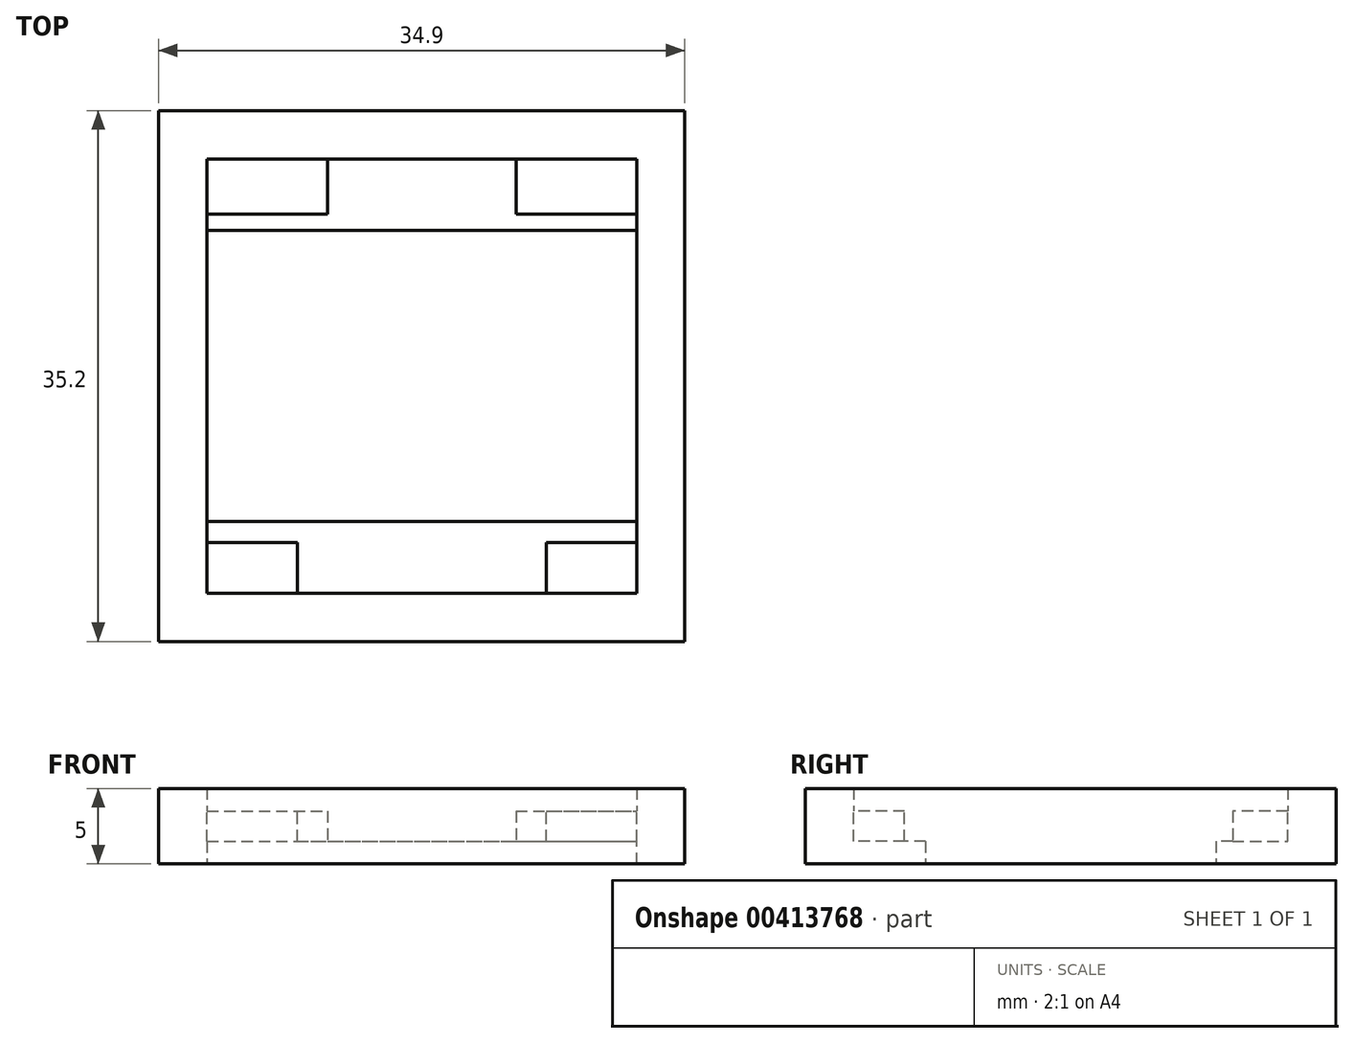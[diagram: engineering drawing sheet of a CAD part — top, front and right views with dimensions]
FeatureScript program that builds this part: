
annotation { "Feature Type Name" : "Feature", "Feature Type Description" : "" }
export const myFeature = defineFeature(function(context is Context, id is Id, definition is map)
    precondition{}
    {
        {
            var Q0;
            Q0=qCreatedBy(makeId("Top.planeOp"),FACE);
            var sketch = newSketch(context, id + "F0", { "sketchPlane" : qUnion([Q0])});
            skLineSegment(sketch, "E0.bottom", {"start": v(-14.25, 14.4) * mm, "end": v(14.25, 14.4) * mm});
            skLineSegment(sketch, "E0.top", {"start": v(-14.25, -14.4) * mm, "end": v(14.25, -14.4) * mm});
            skLineSegment(sketch, "E0.left", {"start": v(-14.25, 14.4) * mm, "end": v(-14.25, -14.4) * mm});
            skLineSegment(sketch, "E0.right", {"start": v(14.25, 14.4) * mm, "end": v(14.25, -14.4) * mm});
            skPoint(sketch, "E0.middle", {"position": v(0, 0) * mm});
            skLineSegment(sketch, "E1.0", {"start": v(17.45, 17.6) * mm, "end": v(17.45, -17.6) * mm});
            skLineSegment(sketch, "E1.1", {"start": v(-17.45, 17.6) * mm, "end": v(17.45, 17.6) * mm});
            skLineSegment(sketch, "E1.2", {"start": v(-17.45, 17.6) * mm, "end": v(-17.45, -17.6) * mm});
            skLineSegment(sketch, "E1.3", {"start": v(-17.45, -17.6) * mm, "end": v(17.45, -17.6) * mm});
            skCircle(sketch, "E2", {"center": v(11.65, -12.4) * mm, "radius": 1.75 * mm, "construction": true});
            skCircle(sketch, "E3", {"center": v(11.65, 11.4) * mm, "radius": 1.75 * mm, "construction": true});
            skCircle(sketch, "E4", {"center": v(-11.65, 11.4) * mm, "radius": 1.75 * mm, "construction": true});
            skCircle(sketch, "E5", {"center": v(-11.65, -12.4) * mm, "radius": 1.75 * mm, "construction": true});
            skLineSegment(sketch, "E6.bottom", {"start": v(-14.25, 9.65) * mm, "end": v(14.25, 9.65) * mm});
            skLineSegment(sketch, "E6.top", {"start": v(-14.25, -9.63) * mm, "end": v(14.25, -9.63) * mm});
            skLineSegment(sketch, "E6.left", {"start": v(-14.25, 9.65) * mm, "end": v(-14.25, -9.63) * mm});
            skLineSegment(sketch, "E6.right", {"start": v(14.25, 9.65) * mm, "end": v(14.25, -9.63) * mm});
            skSolve(sketch);
        }
        {
            var Q0;
            {var subQ4=sQuery(id+"F0.wireOp",EDGE,"E0.bottom");Q0=makeQuery(id+"F0.imprint","IMPRINT",FACE,{"disambiguationData":[TD([[makeQuery(id+"F0.imprint","IMPRINT",EDGE,{"derivedFrom":subQ4}),1.0]])]});}
            extrude(context, id + "F1", {"entities" : qUnion([Q0]), "depth" : 5 * mm, "offsetDistance" : 25 * mm});
        }
        {
            var Q0;
            Q0=qCreatedBy(makeId("Top.planeOp"),FACE);
            var sketch = newSketch(context, id + "F2", { "sketchPlane" : qUnion([Q0])});
            skLineSegment(sketch, "E7.bottom", {"start": v(-14.25, 14.4) * mm, "end": v(14.25, 14.4) * mm});
            skLineSegment(sketch, "E7.top", {"start": v(-14.25, -14.4) * mm, "end": v(14.25, -14.4) * mm});
            skLineSegment(sketch, "E7.left", {"start": v(-14.25, 14.4) * mm, "end": v(-14.25, -14.4) * mm});
            skLineSegment(sketch, "E7.right", {"start": v(14.25, 14.4) * mm, "end": v(14.25, -14.4) * mm});
            skPoint(sketch, "E7.middle", {"position": v(0, 0) * mm});
            skCircle(sketch, "E8", {"center": v(12.25, -12.4) * mm, "radius": 1.75 * mm, "construction": true});
            skCircle(sketch, "E9", {"center": v(11.05, 11.4) * mm, "radius": 1.75 * mm, "construction": true});
            skCircle(sketch, "E10", {"center": v(-12.25, 11.4) * mm, "radius": 1.75 * mm, "construction": true});
            skCircle(sketch, "E11", {"center": v(-11.05, -12.4) * mm, "radius": 1.75 * mm, "construction": true});
            skLineSegment(sketch, "E12.bottom", {"start": v(-14.25, 9.65) * mm, "end": v(14.25, 9.65) * mm});
            skLineSegment(sketch, "E12.top", {"start": v(-14.25, -9.63) * mm, "end": v(14.25, -9.63) * mm});
            skLineSegment(sketch, "E12.left", {"start": v(-14.25, 9.65) * mm, "end": v(-14.25, -9.63) * mm});
            skLineSegment(sketch, "E12.right", {"start": v(14.25, 9.65) * mm, "end": v(14.25, -9.63) * mm});
            skSolve(sketch);
        }
        {
            var Q0;
            {var subQ0=sQuery(id+"F2.wireOp",EDGE,"E7.bottom");Q0=makeQuery(id+"F2.imprint","IMPRINT",FACE,{"disambiguationData":[TD([[makeQuery(id+"F2.imprint","IMPRINT",EDGE,{"derivedFrom":subQ0}),-1.0]])]});}
            var Q1;
            {var subQ0=sQuery(id+"F2.wireOp",EDGE,"E7.top");Q1=makeQuery(id+"F2.imprint","IMPRINT",FACE,{"disambiguationData":[TD([[makeQuery(id+"F2.imprint","IMPRINT",EDGE,{"derivedFrom":subQ0}),1.0]])]});}
            extrude(context, id + "F3", {"entities" : qUnion([Q0, Q1]), "operationType" : NewBodyOperationType.ADD, "depth" : 3.5 * mm, "offsetDistance" : 25 * mm});
        }
        {
            var Q0;
            Q0=qCreatedBy(makeId("Top.planeOp"),FACE);
            cPlane(context, id + "F4", {"entities" : qUnion([Q0]), "cplaneType" : CPlaneType.OFFSET, "offset" : 3.5 * mm, "width" : 150 * mm, "height" : 150 * mm});
        }
        {
            var Q0;
            Q0=qCreatedBy(id+"F4.planeOp",FACE);
            var sketch = newSketch(context, id + "F5", { "sketchPlane" : qUnion([Q0])});
            skLineSegment(sketch, "E13", {"start": v(-6.25, 27.74) * mm, "end": v(-6.25, -4.9) * mm, "construction": true});
            skLineSegment(sketch, "E14", {"start": v(6.25, 21.83) * mm, "end": v(6.25, 6.4) * mm, "construction": true});
            skLineSegment(sketch, "E15", {"start": v(-8.25, -5.52) * mm, "end": v(-8.25, -18.12) * mm, "construction": true});
            skLineSegment(sketch, "E16", {"start": v(8.25, -5.91) * mm, "end": v(8.25, -17.84) * mm, "construction": true});
            skLineSegment(sketch, "E17.bottom", {"start": v(-6.25, 9.65) * mm, "end": v(6.25, 9.65) * mm});
            skLineSegment(sketch, "E17.top", {"start": v(-6.25, 14.4) * mm, "end": v(6.25, 14.4) * mm});
            skLineSegment(sketch, "E17.left", {"start": v(-6.25, 9.65) * mm, "end": v(-6.25, 14.4) * mm});
            skLineSegment(sketch, "E17.right", {"start": v(6.25, 9.65) * mm, "end": v(6.25, 14.4) * mm});
            skLineSegment(sketch, "E18.bottom", {"start": v(-8.25, -9.63) * mm, "end": v(8.25, -9.63) * mm});
            skLineSegment(sketch, "E18.top", {"start": v(-8.25, -14.4) * mm, "end": v(8.25, -14.4) * mm});
            skLineSegment(sketch, "E18.left", {"start": v(-8.25, -9.63) * mm, "end": v(-8.25, -14.4) * mm});
            skLineSegment(sketch, "E18.right", {"start": v(8.25, -9.63) * mm, "end": v(8.25, -14.4) * mm});
            skSolve(sketch);
        }
        {
            var Q0;
            Q0=qSketchRegion(id+"F5",true);
            extrude(context, id + "F6", {"entities" : qUnion([Q0]), "operationType" : NewBodyOperationType.REMOVE, "oppositeDirection" : true, "depth" : 2 * mm, "offsetDistance" : 25 * mm});
        }
        {
            var Q0;
            Q0=qCreatedBy(id+"F4.planeOp",FACE);
            var sketch = newSketch(context, id + "F7", { "sketchPlane" : qUnion([Q0])});
            skLineSegment(sketch, "E19.bottom", {"start": v(-14.25, 10.74) * mm, "end": v(14.25, 10.74) * mm});
            skLineSegment(sketch, "E19.top", {"start": v(-14.25, 9.54) * mm, "end": v(14.25, 9.54) * mm});
            skLineSegment(sketch, "E19.left", {"start": v(-14.25, 10.74) * mm, "end": v(-14.25, 9.54) * mm});
            skLineSegment(sketch, "E19.right", {"start": v(14.25, 10.74) * mm, "end": v(14.25, 9.54) * mm});
            skLineSegment(sketch, "E20.bottom", {"start": v(-14.25, -9.63) * mm, "end": v(14.25, -9.63) * mm});
            skLineSegment(sketch, "E20.top", {"start": v(-14.25, -11.03) * mm, "end": v(14.25, -11.03) * mm});
            skLineSegment(sketch, "E20.left", {"start": v(-14.25, -9.63) * mm, "end": v(-14.25, -11.03) * mm});
            skLineSegment(sketch, "E20.right", {"start": v(14.25, -9.63) * mm, "end": v(14.25, -11.03) * mm});
            skSolve(sketch);
        }
        {
            var Q0;
            Q0=makeQuery(id+"F7.imprint","IMPRINT",FACE,{"disambiguationData":[TD([[makeQuery(id+"F7.imprint","IMPRINT",EDGE,{"derivedFrom":sQuery(id+"F7.wireOp",EDGE,"E20.bottom")}),-1.0]])]});
            var Q1;
            Q1=makeQuery(id+"F7.imprint","IMPRINT",FACE,{"disambiguationData":[TD([[makeQuery(id+"F7.imprint","IMPRINT",EDGE,{"derivedFrom":sQuery(id+"F7.wireOp",EDGE,"E19.bottom")}),-1.0]])]});
            extrude(context, id + "F8", {"entities" : qUnion([Q0, Q1]), "operationType" : NewBodyOperationType.REMOVE, "oppositeDirection" : true, "depth" : 2 * mm, "offsetDistance" : 25 * mm});
        }
    });
